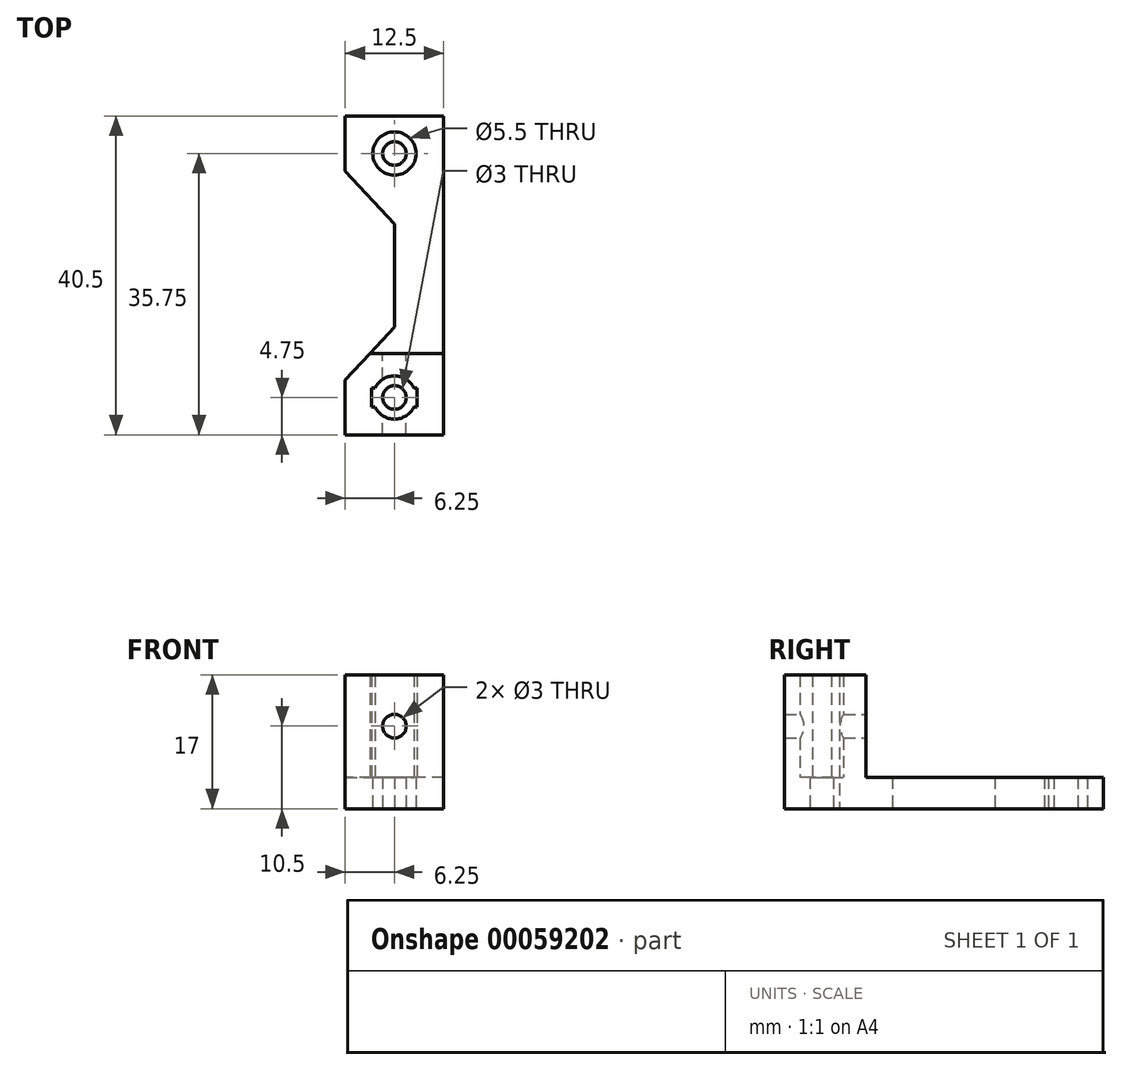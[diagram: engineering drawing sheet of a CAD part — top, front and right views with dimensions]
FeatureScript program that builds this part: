
annotation { "Feature Type Name" : "Feature", "Feature Type Description" : "" }
export const myFeature = defineFeature(function(context is Context, id is Id, definition is map)
    precondition{}
    {
        {
            var Q0;
            Q0=qCreatedBy(makeId("Top.planeOp"),FACE);
            var sketch = newSketch(context, id + "F0", { "sketchPlane" : qUnion([Q0])});
            skLineSegment(sketch, "E0.rect.bottom", {"start": v(6.25, -20.25) * mm, "end": v(-6.25, -20.25) * mm});
            skLineSegment(sketch, "E0.rect.top", {"start": v(6.25, 20.25) * mm, "end": v(-6.25, 20.25) * mm});
            skLineSegment(sketch, "E0.rect.left", {"start": v(6.25, -20.25) * mm, "end": v(6.25, 20.25) * mm});
            skLineSegment(sketch, "E0.rect.right", {"start": v(-6.25, -20.25) * mm, "end": v(-6.25, -13.25) * mm});
            skPoint(sketch, "E0.rect.middle", {"position": v(0, 0) * mm});
            skLineSegment(sketch, "E1", {"start": v(0, 0) * mm, "end": v(0, -6.52) * mm});
            skCircle(sketch, "E2", {"center": v(0, -15.5) * mm, "radius": 1.5 * mm});
            skLineSegment(sketch, "E3", {"start": v(-6.25, -13.25) * mm, "end": v(0, -6.52) * mm});
            skLineSegment(sketch, "E4.MirrorCS", {"start": v(0, 0) * mm, "end": v(0, 6.52) * mm});
            skLineSegment(sketch, "E5.MirrorCS", {"start": v(-6.25, 13.25) * mm, "end": v(0, 6.52) * mm});
            skCircle(sketch, "E6.MirrorC", {"center": v(0, 15.5) * mm, "radius": 1.5 * mm});
            skLineSegment(sketch, "E7.trimOffspring", {"start": v(-6.25, 13.25) * mm, "end": v(-6.25, 20.25) * mm});
            skLineSegment(sketch, "E8", {"start": v(0, -6.52) * mm, "end": v(6.25, -6.52) * mm});
            skCircle(sketch, "E9", {"center": v(0, -15.5) * mm, "radius": 2.75 * mm});
            skCircle(sketch, "E10", {"center": v(0, 15.5) * mm, "radius": 2.75 * mm});
            skLineSegment(sketch, "E11", {"start": v(-3.12, -9.88) * mm, "end": v(6.25, -9.88) * mm});
            skLineSegment(sketch, "E12", {"start": v(0, -15.5) * mm, "end": v(2.9, -15.5) * mm, "construction": true});
            skLineSegment(sketch, "E13", {"start": v(2.9, -15.5) * mm, "end": v(2.9, -16.7) * mm, "construction": true});
            skLineSegment(sketch, "E14", {"start": v(0, -15.5) * mm, "end": v(0, -20.25) * mm, "construction": true});
            skLineSegment(sketch, "E15", {"start": v(0, -15.5) * mm, "end": v(-2.9, -15.5) * mm, "construction": true});
            skLineSegment(sketch, "E16", {"start": v(-2.9, -15.5) * mm, "end": v(-2.9, -14.3) * mm, "construction": true});
            skLineSegment(sketch, "E17.bottom", {"start": v(-2.9, -14.3) * mm, "end": v(2.9, -14.3) * mm});
            skLineSegment(sketch, "E17.top", {"start": v(-2.9, -16.7) * mm, "end": v(2.9, -16.7) * mm});
            skLineSegment(sketch, "E17.left", {"start": v(-2.9, -14.3) * mm, "end": v(-2.9, -16.7) * mm});
            skLineSegment(sketch, "E17.right", {"start": v(2.9, -14.3) * mm, "end": v(2.9, -16.7) * mm});
            skSolve(sketch);
        }
        {
            var Q0;
            Q0 = qSketchRegion(id + "F0", true);
            var Q1;
            Q1=makeQuery(id+"F0.imprint","IMPRINT",FACE,{"disambiguationData":[TD([[makeQuery(id+"F0.imprint","IMPRINT",EDGE,{"derivedFrom":sQuery(id+"F0.wireOp",EDGE,"E6.MirrorC")}),1.0]])]});
            var Q2;
            Q2=makeQuery(id+"F0.imprint","IMPRINT",FACE,{"disambiguationData":[TD([[makeQuery(id+"F0.imprint","IMPRINT",EDGE,{"derivedFrom":sQuery(id+"F0.wireOp",EDGE,"E2")}),-1.0]])]});
            var Q3;
            {var subQ5=sQuery(id+"F0.wireOp",EDGE,"E17.left");Q3=makeQuery(id+"F0.imprint","IMPRINT",FACE,{"disambiguationData":[TD([[makeQuery(id+"F0.imprint","IMPRINT",EDGE,{"derivedFrom":subQ5}),1.0]])]});}
            var Q4;
            {var subQ5=sQuery(id+"F0.wireOp",EDGE,"E17.right");Q4=makeQuery(id+"F0.imprint","IMPRINT",FACE,{"disambiguationData":[TD([[makeQuery(id+"F0.imprint","IMPRINT",EDGE,{"derivedFrom":subQ5}),-1.0]])]});}
            extrude(context, id + "F1", {"entities" : qUnion([Q0, Q1, Q2, Q3, Q4]), "depth" : 4 * mm});
        }
        {
            var Q0;
            {var subQ2=sQuery(id+"F0.wireOp",EDGE,"E0.rect.bottom");Q0=makeQuery(id+"F0.imprint","IMPRINT",FACE,{"disambiguationData":[TD([[makeQuery(id+"F0.imprint","IMPRINT",EDGE,{"derivedFrom":subQ2}),-1.0]])]});}
            extrude(context, id + "F2", {"entities" : qUnion([Q0]), "operationType" : NewBodyOperationType.ADD, "depth" : 17 * mm});
        }
        {
            var Q0;
            Q0=qCreatedBy(makeId("Front.planeOp"),FACE);
            var sketch = newSketch(context, id + "F3", { "sketchPlane" : qUnion([Q0])});
            skLineSegment(sketch, "E18", {"start": v(0, 0) * mm, "end": v(0, 10.5) * mm});
            skCircle(sketch, "E19", {"center": v(0, 10.5) * mm, "radius": 1.5 * mm});
            skSolve(sketch);
        }
        {
            var Q0;
            Q0 = qSketchRegion(id + "F3", true);
            extrude(context, id + "F4", {"entities" : qUnion([Q0]), "operationType" : NewBodyOperationType.REMOVE, "depth" : 25 * mm});
        }
    });
